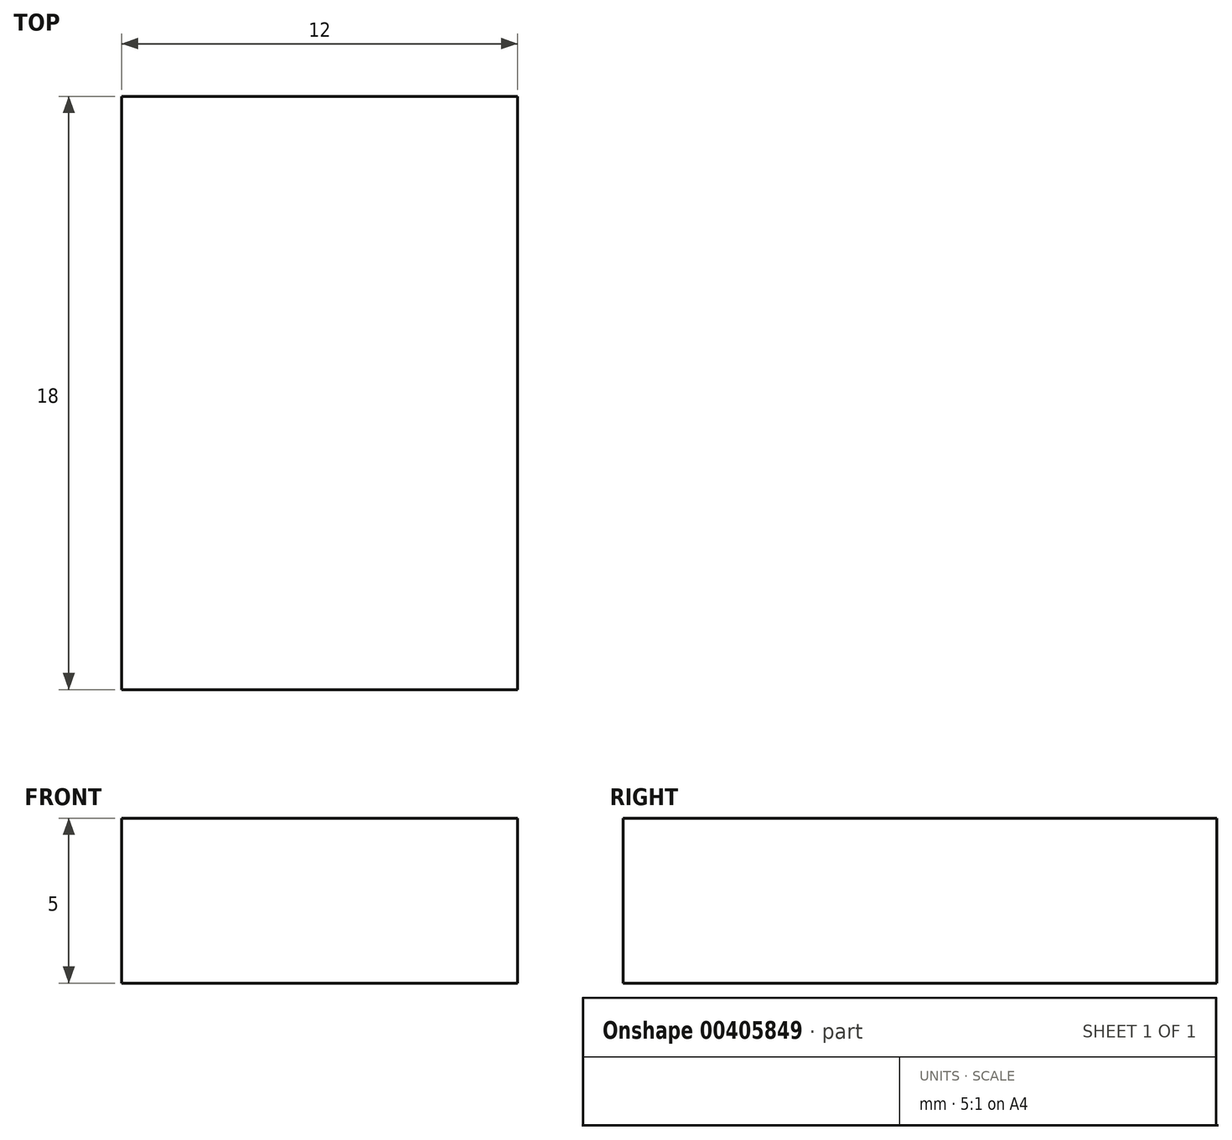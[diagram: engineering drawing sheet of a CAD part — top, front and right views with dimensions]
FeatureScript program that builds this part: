
annotation { "Feature Type Name" : "Feature", "Feature Type Description" : "" }
export const myFeature = defineFeature(function(context is Context, id is Id, definition is map)
    precondition{}
    {
        {
            var Q0;
            Q0=qCreatedBy(makeId("Top.planeOp"),FACE);
            var sketch = newSketch(context, id + "F0", { "sketchPlane" : qUnion([Q0])});
            skLineSegment(sketch, "E0.bottom", {"start": v(-35.52, -23.86) * mm, "end": v(-23.52, -23.86) * mm});
            skLineSegment(sketch, "E0.top", {"start": v(-35.52, -5.86) * mm, "end": v(-23.52, -5.86) * mm});
            skLineSegment(sketch, "E0.left", {"start": v(-35.52, -23.86) * mm, "end": v(-35.52, -5.86) * mm});
            skLineSegment(sketch, "E0.right", {"start": v(-23.52, -23.86) * mm, "end": v(-23.52, -5.86) * mm});
            skSolve(sketch);
        }
        {
            var Q0;
            Q0=makeQuery(id+"F0.imprint","IMPRINT",FACE,{"disambiguationData":[TD([[makeQuery(id+"F0.imprint","IMPRINT",EDGE,{"derivedFrom":sQuery(id+"F0.wireOp",EDGE,"E0.bottom")}),1.0]])]});
            extrude(context, id + "F1", {"entities" : qUnion([Q0]), "depth" : 5 * mm});
        }
    });
